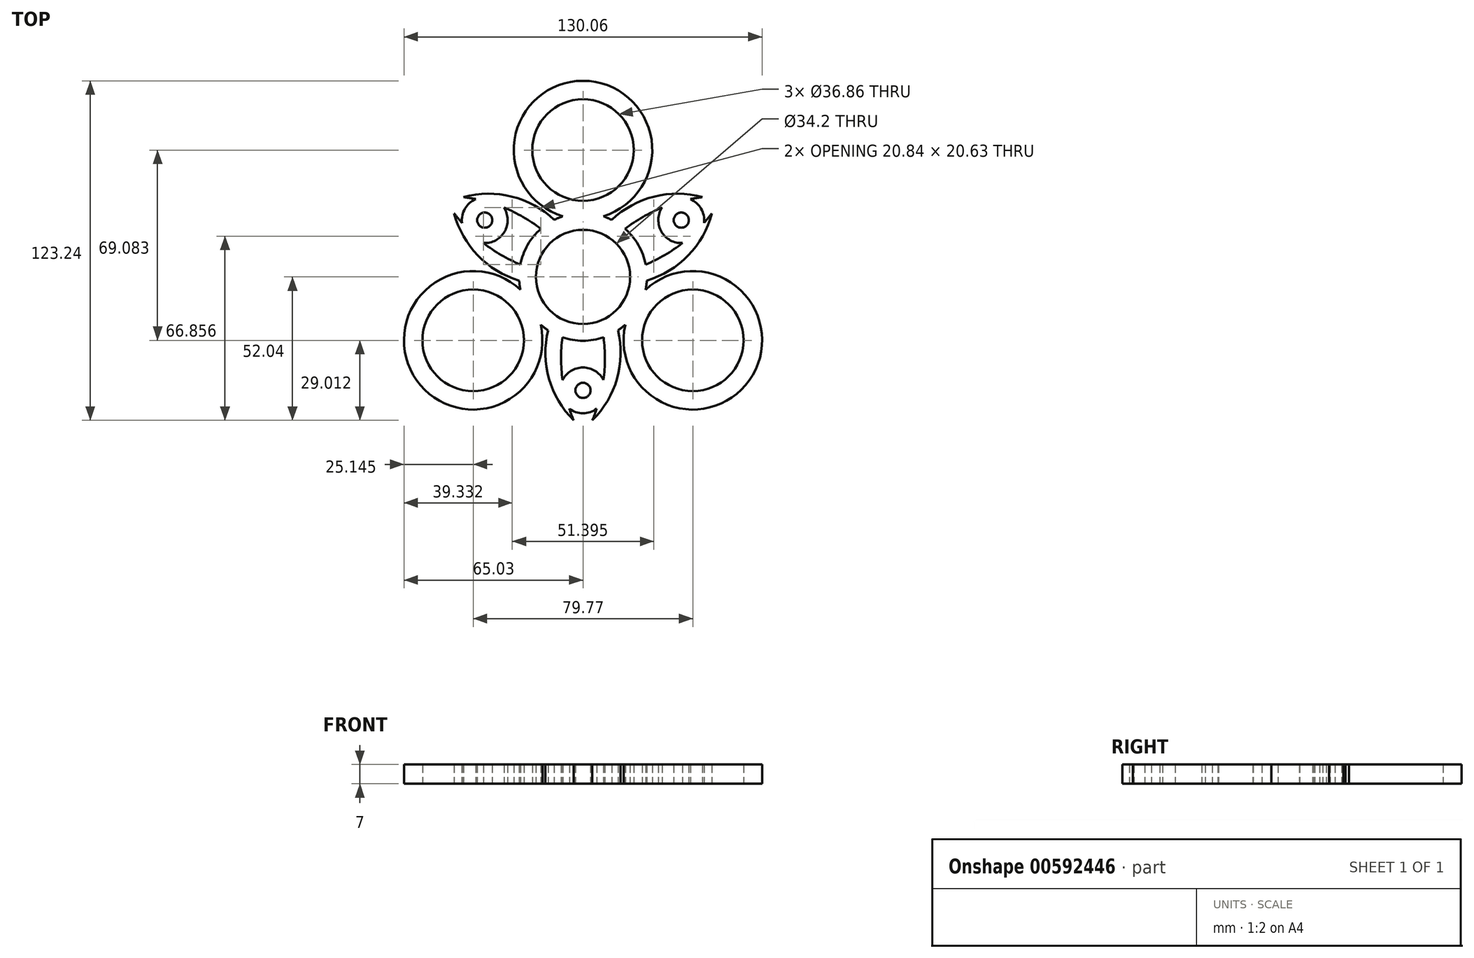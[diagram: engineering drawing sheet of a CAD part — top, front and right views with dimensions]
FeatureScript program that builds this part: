
annotation { "Feature Type Name" : "Feature", "Feature Type Description" : "" }
export const myFeature = defineFeature(function(context is Context, id is Id, definition is map)
    precondition{}
    {
        {
            var Q0;
            Q0=qCreatedBy(makeId("Top.planeOp"),FACE);
            var sketch = newSketch(context, id + "F0", { "sketchPlane" : qUnion([Q0])});
            skCircle(sketch, "E0", {"center": v(0, 0) * mm, "radius": 17.1 * mm});
            skArc(sketch, "E1", {"start": v(22.76, 4.5) * mm, "mid": v(17.41, 15.33) * mm, "end": v(7.34, 22) * mm});
            skCircle(sketch, "E2", {"center": v(0, 46.06) * mm, "radius": 18.43 * mm});
            skArc(sketch, "E3", {"start": v(7.34, 22) * mm, "mid": v(0, 71.2) * mm, "end": v(-7.34, 22) * mm});
            skArc(sketch, "E4.1.0", {"start": v(-22.73, -4.64) * mm, "mid": v(-61.66, -35.6) * mm, "end": v(-15.39, -17.36) * mm});
            skCircle(sketch, "E4.1.1", {"center": v(-39.89, -23.03) * mm, "radius": 18.43 * mm});
            skArc(sketch, "E4.2.0", {"start": v(15.39, -17.36) * mm, "mid": v(61.66, -35.6) * mm, "end": v(22.73, -4.64) * mm});
            skCircle(sketch, "E4.2.1", {"center": v(39.89, -23.03) * mm, "radius": 18.43 * mm});
            skArc(sketch, "E5", {"start": v(23.16, -1.3) * mm, "mid": v(38.18, 7.78) * mm, "end": v(46.77, 23.07) * mm});
            skArc(sketch, "E6", {"start": v(22.76, 4.5) * mm, "mid": v(29.7, 7.95) * mm, "end": v(36.12, 12.3) * mm});
            skArc(sketch, "E7.trimOffspring", {"start": v(22.73, -4.64) * mm, "mid": v(23, -2.98) * mm, "end": v(23.16, -1.3) * mm});
            skArc(sketch, "E8.trimOffspring", {"start": v(-15.39, -17.36) * mm, "mid": v(-14.09, -18.43) * mm, "end": v(-12.71, -19.4) * mm});
            skArc(sketch, "E9.trimOffspring", {"start": v(-7.34, 22) * mm, "mid": v(-8.92, 21.42) * mm, "end": v(-10.45, 20.71) * mm});
            skArc(sketch, "E10.1.0", {"start": v(-10.45, 20.71) * mm, "mid": v(-25.82, 29.17) * mm, "end": v(-43.37, 28.97) * mm});
            skArc(sketch, "E10.1.1", {"start": v(-15.28, 17.46) * mm, "mid": v(-21.74, 21.74) * mm, "end": v(-28.7, 25.13) * mm});
            skArc(sketch, "E10.2.0", {"start": v(-12.71, -19.4) * mm, "mid": v(-12.35, -36.95) * mm, "end": v(-3.4, -52.04) * mm});
            skArc(sketch, "E10.2.1", {"start": v(-7.48, -21.96) * mm, "mid": v(-7.96, -29.7) * mm, "end": v(-7.41, -37.43) * mm});
            skArc(sketch, "E11.trimOffspring", {"start": v(-15.28, 17.46) * mm, "mid": v(-21.98, 7.41) * mm, "end": v(-22.73, -4.64) * mm});
            skArc(sketch, "E12.trimOffspring", {"start": v(-7.48, -21.96) * mm, "mid": v(4.57, -22.74) * mm, "end": v(15.39, -17.36) * mm});
            skArc(sketch, "E13.MirrorCS", {"start": v(7.48, -21.96) * mm, "mid": v(7.96, -29.7) * mm, "end": v(7.41, -37.43) * mm});
            skArc(sketch, "E14.MirrorCS", {"start": v(12.71, -19.4) * mm, "mid": v(12.35, -36.95) * mm, "end": v(3.4, -52.04) * mm});
            skArc(sketch, "E15.1.0", {"start": v(15.28, 17.46) * mm, "mid": v(21.74, 21.74) * mm, "end": v(28.7, 25.13) * mm});
            skArc(sketch, "E15.2.0", {"start": v(-22.76, 4.5) * mm, "mid": v(-29.7, 7.95) * mm, "end": v(-36.12, 12.3) * mm});
            skArc(sketch, "E16.1.0", {"start": v(10.45, 20.71) * mm, "mid": v(25.82, 29.17) * mm, "end": v(43.37, 28.97) * mm});
            skArc(sketch, "E16.2.0", {"start": v(-23.16, -1.3) * mm, "mid": v(-38.18, 7.78) * mm, "end": v(-46.77, 23.07) * mm});
            skPoint(sketch, "E17.center.orphan", {"position": v(0, -43.34) * mm});
            skCircle(sketch, "E18", {"center": v(0, -41.2) * mm, "radius": 8.32 * mm});
            skArc(sketch, "E19.trimOffspring", {"start": v(-4.97, -47.88) * mm, "mid": v(-4.23, -49.98) * mm, "end": v(-3.4, -52.04) * mm});
            skArc(sketch, "E20.trimOffspring", {"start": v(4.97, -47.88) * mm, "mid": v(4.23, -49.98) * mm, "end": v(3.4, -52.04) * mm});
            skCircle(sketch, "E21.1.0", {"center": v(35.69, 20.6) * mm, "radius": 8.32 * mm});
            skCircle(sketch, "E21.2.0", {"center": v(-35.69, 20.6) * mm, "radius": 8.32 * mm});
            skArc(sketch, "E22.trimOffspring", {"start": v(-43.95, 19.63) * mm, "mid": v(-45.4, 21.33) * mm, "end": v(-46.77, 23.07) * mm});
            skArc(sketch, "E23.trimOffspring", {"start": v(-38.98, 28.24) * mm, "mid": v(-41.17, 28.65) * mm, "end": v(-43.37, 28.97) * mm});
            skArc(sketch, "E24.trimOffspring", {"start": v(38.98, 28.24) * mm, "mid": v(41.17, 28.65) * mm, "end": v(43.37, 28.97) * mm});
            skArc(sketch, "E25.trimOffspring", {"start": v(43.95, 19.63) * mm, "mid": v(45.4, 21.33) * mm, "end": v(46.77, 23.07) * mm});
            skCircle(sketch, "E26", {"center": v(35.69, 20.6) * mm, "radius": 2.75 * mm});
            skCircle(sketch, "E27.1.0", {"center": v(-35.69, 20.6) * mm, "radius": 2.75 * mm});
            skCircle(sketch, "E27.2.0", {"center": v(0, -41.2) * mm, "radius": 2.75 * mm});
            skSolve(sketch);
        }
        {
            var Q0;
            Q0 = qSketchRegion(id + "F0", true);
            extrude(context, id + "F1", {"entities" : qUnion([Q0]), "depth" : 7 * mm, "offsetDistance" : 25 * mm});
        }
    });
